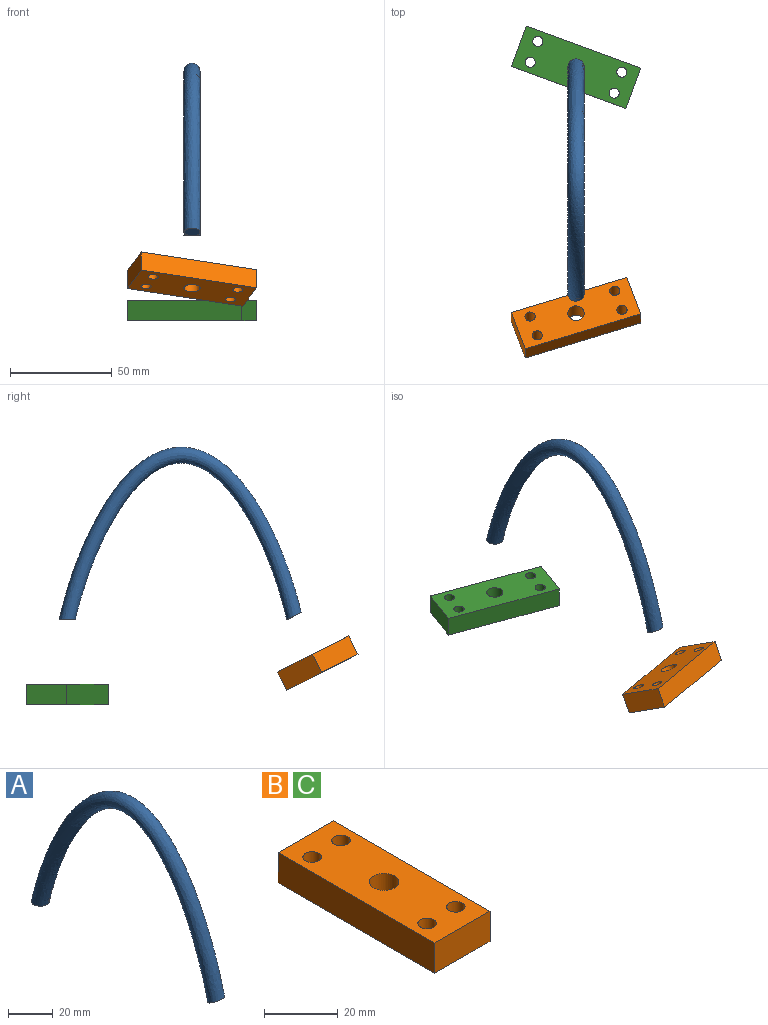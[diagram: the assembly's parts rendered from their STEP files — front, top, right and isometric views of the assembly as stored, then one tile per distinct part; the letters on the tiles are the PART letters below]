
ASSEMBLY  parts=3 mates=2
PART A: 3 faces, bbox 8x126.7x90.9 mm
  f0: plane 8x8mm, normal (0,0,-1), area 50.3mm2, adj f2
  f1: plane 8x7.14mm, normal (0,-0.45,-0.89), area 50.3mm2, adj f2
  f2: bspline ~126.71x90.87mm, area 5122.6mm2, adj f0,f1
PART B: 11 faces, bbox 21.2x60x10 mm
  f0: plane 21.15x10mm, normal (0,-1,0), area 211.5mm2, adj f1,f3,f9,f10
  f1: plane 60x10mm, normal (1,0,0), area 600mm2, adj f0,f2,f9,f10
  f2: plane 21.15x10mm, normal (0,1,0), area 211.5mm2, adj f1,f3,f9,f10
  f3: plane 60x10mm, normal (-1,0,0), area 600mm2, adj f0,f2,f9,f10
  f4: cylinder r=2.5mm len=10mm, axis (0,0,-1), area 157.1mm2, adj f9,f10
  f5: cylinder r=2.5mm len=10mm, axis (0,0,-1), area 157.1mm2, adj f9,f10
  f6: cylinder r=2.5mm len=10mm, axis (0,0,-1), area 157.1mm2, adj f9,f10
  f7: cylinder r=4mm len=10mm, axis (0,0,-1), area 251.3mm2, adj f9,f10
  f8: cylinder r=2.5mm len=10mm, axis (0,0,-1), area 157.1mm2, adj f9,f10
  f9: plane 60x21.15mm, normal (0,0,1), area 1140.5mm2, adj f0,f1,f2,f3,f4,f5,f6,f7
  f10: plane 60x21.15mm, normal (0,0,-1), area 1140.5mm2, adj f0,f1,f2,f3,f4,f5,f6,f7
PART C: same geometry as B
PLACE A t=(-43.99,120.26,-0.94)mm fixed
PLACE B rot(axis=(-0.31,-0.22,-0.93),75.5deg) t=(-43.99,50.73,-26.75)mm
PLACE C rot(axis=(0,0,-1),110.1deg) t=(-43.99,176.26,-42.8)mm
MATE cylindrical C.f7 <-> A.f0  axis (0,0,1) through (-43.99,176.26,-32.8)mm
MATE cylindrical B.f7 <-> A.f1  axis (0,0.45,0.89) through (-43.99,55.25,-17.82)mm
